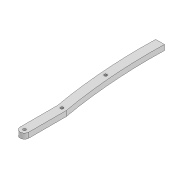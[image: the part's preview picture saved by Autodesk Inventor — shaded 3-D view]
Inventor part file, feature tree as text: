
AUTODESK INVENTOR PART (.ipt)
format: ipt  version: 2022 (Build 260153000, 153)  size: 117,248 bytes
history: native  units: mm
features: extrude x2, sketch x1
ambient origin geometry x8: Origin, YZ Plane, XZ Plane, XY Plane, X Axis, Y Axis, Z Axis, Center Point
bodies: Solid1 (feature_tree)
feature tree (3):
  extrude  "Extrusion1"  Depth=10.0mm
  extrude  "Extrusion2"  Depth=10.0mm
  sketch  "Sketch2"  dims[d0=3.3mm d1=3.3mm d2=10.0mm d3=312.648mm d6=6.0mm d7=0.0mm d10=3.3mm d11=42.6mm d12=3.3mm d13=254.274mm d16=600.0mm d17=600.0mm d18=3.3mm d19=100.0mm d20=10.0mm d21=0.0mm]
